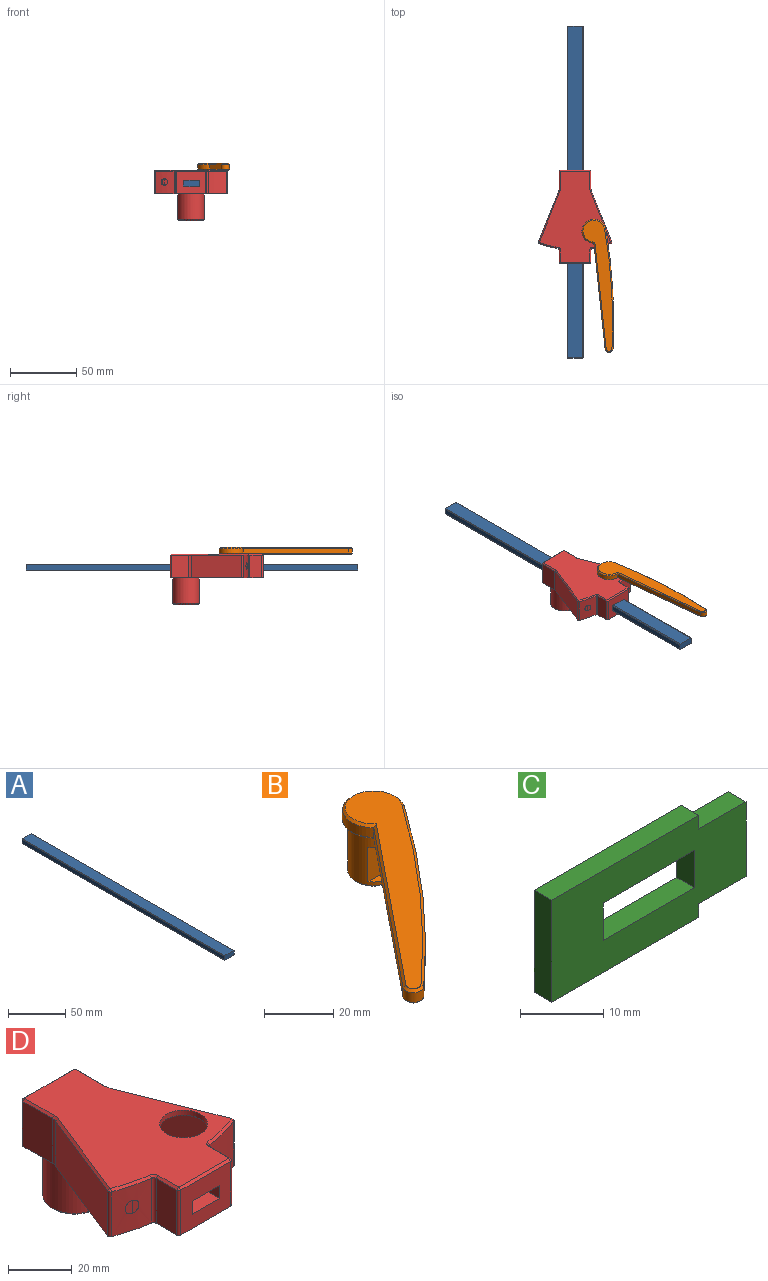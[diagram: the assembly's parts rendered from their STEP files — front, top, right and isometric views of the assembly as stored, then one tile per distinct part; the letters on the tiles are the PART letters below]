
ASSEMBLY  parts=4 mates=3
PART A: 10 faces, bbox 12x250x5 mm
  f0: plane 250x11mm, normal (0,0,-1), area 2750mm2, adj f4,f5,f6,f9
  f1: plane 250x4mm, normal (1,0,0), area 1000mm2, adj f4,f5,f6,f7
  f2: plane 250x11mm, normal (0,0,1), area 2750mm2, adj f4,f5,f7,f8
  f3: plane 250x4mm, normal (-1,0,0), area 1000mm2, adj f4,f5,f8,f9
  f4: plane 12x5mm, normal (0,-1,0), area 59.8mm2, adj f0,f1,f2,f3,f6,f7,f8,f9
  f5: plane 12x5mm, normal (0,1,0), area 59.8mm2, adj f0,f1,f2,f3,f6,f7,f8,f9
  f6: cylinder r=0.5mm len=250mm, axis (0,-1,0), area 196.3mm2, adj f0,f1,f4,f5
  f7: cylinder r=0.5mm len=250mm, axis (0,1,0), area 196.3mm2, adj f1,f2,f4,f5
  f8: cylinder r=0.5mm len=250mm, axis (0,-1,0), area 196.3mm2, adj f2,f3,f4,f5
  f9: cylinder r=0.5mm len=250mm, axis (0,1,0), area 196.3mm2, adj f0,f3,f4,f5
PART B: 21 faces, bbox 66.3x82.5x23 mm
  f0: cylinder r=7.5mm len=17.2mm, axis (0,0,1), area 437mm2, adj f2,f3,f4,f5,f11,f16
  f1: plane 13.4x13.4mm, normal (0,0,-1), area 141mm2, adj f16
  f2: plane 12x6.34mm, normal (0,-1,0), area 76.1mm2, adj f0,f3,f4,f5
  f3: cylinder r=5.75mm len=12mm, axis (0,0,-1), area 216.8mm2, adj f0,f2,f4,f5
  f4: plane 15x13.84mm, normal (0,0,-1), area 52.1mm2, adj f0,f2,f3
  f5: plane 15x13.84mm, normal (0,0,1), area 52.1mm2, adj f0,f2,f3
  f6: cylinder r=400mm len=67.53mm, axis (0,0,-1), area 307.1mm2, adj f7,f9,f12,f20
  f7: cylinder r=9mm len=18mm, axis (0,0,-1), area 138.9mm2, adj f6,f8,f14,f18
  f8: plane 62.22x50.29mm, normal (-0.78,0.63,0), area 272mm2, adj f7,f9,f15,f17
  f9: cylinder r=3mm len=5.01mm, axis (0,0,-1), area 30.4mm2, adj f6,f8,f13,f19
  f10: plane 80.87x64.72mm, normal (0,0,1), area 881.8mm2, adj f17,f18,f19,f20
  f11: plane 80.87x64.72mm, normal (0,0,-1), area 705.1mm2, adj f0,f12,f13,f14,f15
  f12: cone r=399.2mm half-angle=45deg, axis (0,0,1), area 102.1mm2, adj f6,f11,f13,f14
  f13: cone r=2.2mm half-angle=45deg, axis (0,0,1), area 8.8mm2, adj f9,f11,f12,f15
  f14: cone r=9mm half-angle=45deg, axis (0,0,1), area 44.6mm2, adj f7,f11,f12,f15
  f15: plane 62.8x51.38mm, normal (-0.55,0.44,-0.71), area 90.9mm2, adj f8,f11,f13,f14
  f16: cone r=7.5mm half-angle=45deg, axis (0,0,1), area 50.5mm2, adj f0,f1
  f17: plane 62.8x51.38mm, normal (-0.55,0.44,0.71), area 90.9mm2, adj f8,f10,f18,f19
  f18: cone r=8.2mm half-angle=45deg, axis (0,0,-1), area 44.6mm2, adj f7,f10,f17,f20
  f19: cone r=3mm half-angle=45deg, axis (0,0,-1), area 8.8mm2, adj f9,f10,f17,f20
  f20: cone r=400mm half-angle=45deg, axis (0,0,-1), area 102.1mm2, adj f6,f10,f18,f19
PART C: 14 faces, bbox 33x3x15 mm
  f0: plane 15.5x3mm, normal (0,0,-1), area 46.5mm2, adj f1,f11,f12,f13
  f1: plane 5.5x3mm, normal (-1,0,0), area 16.5mm2, adj f0,f2,f12,f13
  f2: plane 15.5x3mm, normal (0,0,1), area 46.5mm2, adj f1,f11,f12,f13
  f3: plane 25x3mm, normal (0,0,-1), area 75mm2, adj f4,f10,f12,f13
  f4: plane 3x2mm, normal (1,0,0), area 6mm2, adj f3,f5,f12,f13
  f5: plane 8x3mm, normal (0,0,-1), area 24mm2, adj f4,f6,f12,f13
  f6: plane 11x3mm, normal (1,0,0), area 33mm2, adj f5,f7,f12,f13
  f7: plane 8x3mm, normal (0,0,1), area 24mm2, adj f6,f8,f12,f13
  f8: plane 3x2mm, normal (1,0,0), area 6mm2, adj f7,f9,f12,f13
  f9: plane 25x3mm, normal (0,0,1), area 75mm2, adj f8,f10,f12,f13
  f10: plane 15x3mm, normal (-1,0,0), area 45mm2, adj f3,f9,f12,f13
  f11: plane 5.5x3mm, normal (1,0,0), area 16.5mm2, adj f0,f2,f12,f13
  f12: plane 33x15mm, normal (0,-1,0), area 377.7mm2, adj f0,f1,f2,f3,f4,f5,f6,f7
  f13: plane 33x15mm, normal (0,1,0), area 377.7mm2, adj f0,f1,f2,f3,f4,f5,f6,f7
PART D: 63 faces, bbox 55.6x70.3x38.3 mm
  f0: cylinder r=80mm len=17.2mm, axis (0,0,-1), area 232.7mm2, adj f7,f30,f31,f33,f38,f46
  f1: plane 16x4.49mm, normal (0,1,0), area 71.8mm2, adj f2,f7,f17,f29
  f2: plane 7.79x4.49mm, normal (0,0,-1), area 11.4mm2, adj f1,f17,f29
  f3: plane 22x17.2mm, normal (0,-1,0), area 318.4mm2, adj f7,f23,f24,f25,f26,f34,f37,f45
  f4: plane 22x17.2mm, normal (0,1,0), area 318.4mm2, adj f7,f19,f20,f21,f22,f35,f36,f58
  f5: plane 33.09x16.26mm, normal (0,1,0), area 439.1mm2, adj f7,f16,f18,f23,f24,f25,f26,f29
  f6: plane 26.09x16mm, normal (0,-1,0), area 357.5mm2, adj f7,f16,f17,f18,f19,f20,f21,f22
  f7: plane 70x55.38mm, normal (0,0,-1), area 1017.3mm2, adj f0,f1,f3,f4,f5,f6,f8,f9
  f8: cylinder r=80mm len=17.2mm, axis (0,0,-1), area 252.4mm2, adj f7,f32,f39,f53
  f9: plane 38.15x17.2mm, normal (0.93,0.37,0), area 706.7mm2, adj f7,f39,f40,f57
  f10: plane 38.15x17.2mm, normal (-0.93,0.37,0), area 706.7mm2, adj f7,f38,f41,f50
  f11: plane 68.4x53.78mm, normal (0,0,1), area 2047.7mm2, adj f29,f42,f43,f44,f45,f46,f47,f48
  f12: plane 17.2x8.99mm, normal (1,0,0), area 154.6mm2, adj f7,f32,f34,f49
  f13: plane 17.2x8.99mm, normal (-1,0,0), area 154.6mm2, adj f7,f33,f37,f42
  f14: plane 17.2x13.04mm, normal (1,0,0), area 224.2mm2, adj f7,f35,f40,f61
  f15: plane 17.2x13.04mm, normal (-1,0,0), area 224.2mm2, adj f7,f36,f41,f54
  f16: plane 28x16mm, normal (0.93,-0.37,0), area 482.5mm2, adj f5,f6,f7,f18
  f17: plane 28x16mm, normal (-0.93,-0.37,0), area 482.5mm2, adj f1,f2,f6,f7,f18
  f18: plane 45.38x28mm, normal (0,0,-1), area 875.4mm2, adj f5,f6,f16,f17,f29
  f19: plane 23x5mm, normal (1,0,0), area 115mm2, adj f4,f6,f20,f22
  f20: plane 23x12mm, normal (0,0,-1), area 276mm2, adj f4,f6,f19,f21
  f21: plane 23x5mm, normal (-1,0,0), area 115mm2, adj f4,f6,f20,f22
  f22: plane 23x12mm, normal (0,0,1), area 276mm2, adj f4,f6,f19,f21
  f23: plane 19x12mm, normal (0,0,1), area 228mm2, adj f3,f5,f24,f26
  f24: plane 19x5mm, normal (-1,0,0), area 95mm2, adj f3,f5,f23,f25
  f25: plane 19x12mm, normal (0,0,-1), area 228mm2, adj f3,f5,f24,f26
  f26: plane 19x5mm, normal (1,0,0), area 95mm2, adj f3,f5,f23,f25
  f27: cylinder r=10mm len=20mm, axis (0,0,1), area 1206.4mm2, adj f7,f62
  f28: plane 18.4x18.4mm, normal (0,0,-1), area 265.9mm2, adj f62
  f29: cylinder r=7.5mm len=18mm, axis (0,0,-1), area 296.1mm2, adj f1,f2,f5,f7,f11,f18
  f30: cone r=2.5mm half-angle=3deg, axis (0.21,0.98,0), area 111.5mm2, adj f0,f5,f31
  f31: cylinder r=2.5mm len=5mm, axis (-0.21,-0.98,0), area 0mm2, adj f0,f30
  f32: cylinder r=1mm len=17.2mm, axis (0,0,-1), area 24.2mm2, adj f7,f8,f12,f51
  f33: cylinder r=1mm len=17.2mm, axis (0,0,-1), area 24.2mm2, adj f0,f7,f13,f44
  f34: cylinder r=1mm len=17.2mm, axis (0,0,1), area 27mm2, adj f3,f7,f12,f47
  f35: cylinder r=1mm len=17.2mm, axis (0,0,-1), area 27mm2, adj f4,f7,f14,f60
  f36: cylinder r=1mm len=17.2mm, axis (0,0,1), area 27mm2, adj f4,f7,f15,f56
  f37: cylinder r=1mm len=17.2mm, axis (0,0,-1), area 27mm2, adj f3,f7,f13,f43
  f38: cylinder r=1mm len=17.2mm, axis (0,0,-1), area 27.6mm2, adj f0,f7,f10,f48
  f39: cylinder r=1mm len=17.2mm, axis (0,0,-1), area 27.6mm2, adj f7,f8,f9,f55
  f40: cylinder r=5mm len=17.2mm, axis (0,0,1), area 32.7mm2, adj f7,f9,f14,f59
  f41: cylinder r=5mm len=17.2mm, axis (0,0,1), area 32.7mm2, adj f7,f10,f15,f52
  f42: plane 8.99x0.8mm, normal (-0.71,0,0.71), area 10.2mm2, adj f11,f13,f43,f44
  f43: cone r=0.2mm half-angle=45deg, axis (0,0,-1), area 1.1mm2, adj f11,f37,f42,f45
  f44: cone r=1.8mm half-angle=45deg, axis (0,0,1), area 2.2mm2, adj f11,f33,f42,f46
  f45: plane 22x0.8mm, normal (0,-0.71,0.71), area 24.9mm2, adj f3,f11,f43,f47
  f46: cone r=79.2mm half-angle=45deg, axis (0,0,-1), area 16.5mm2, adj f0,f11,f44,f48
  f47: cone r=0.2mm half-angle=45deg, axis (0,0,-1), area 1.1mm2, adj f11,f34,f45,f49
  f48: cone r=0.2mm half-angle=45deg, axis (0,0,-1), area 1.1mm2, adj f11,f38,f46,f50
  f49: plane 8.99x0.8mm, normal (0.71,0,0.71), area 10.2mm2, adj f11,f12,f47,f51
  f50: plane 38.45x16mm, normal (-0.66,0.26,0.71), area 46.5mm2, adj f10,f11,f48,f52
  f51: cone r=1.8mm half-angle=45deg, axis (0,0,1), area 2.2mm2, adj f11,f32,f49,f53
  f52: cone r=5.8mm half-angle=45deg, axis (0,0,1), area 2.3mm2, adj f11,f41,f50,f54
  f53: cone r=79.2mm half-angle=45deg, axis (0,0,-1), area 16.5mm2, adj f8,f11,f51,f55
  f54: plane 13.04x0.8mm, normal (-0.71,0,0.71), area 14.7mm2, adj f11,f15,f52,f56
  f55: cone r=0.2mm half-angle=45deg, axis (0,0,-1), area 1.1mm2, adj f11,f39,f53,f57
  f56: cone r=0.2mm half-angle=45deg, axis (0,0,-1), area 1.1mm2, adj f11,f36,f54,f58
  f57: plane 38.45x16mm, normal (0.66,0.26,0.71), area 46.5mm2, adj f9,f11,f55,f59
  f58: plane 22x0.8mm, normal (0,0.71,0.71), area 24.9mm2, adj f4,f11,f56,f60
  f59: cone r=5.8mm half-angle=45deg, axis (0,0,1), area 2.3mm2, adj f11,f40,f57,f61
  f60: cone r=0.2mm half-angle=45deg, axis (0,0,-1), area 1.1mm2, adj f11,f35,f58,f61
  f61: plane 13.04x0.8mm, normal (0.71,0,0.71), area 14.7mm2, adj f11,f14,f59,f60
  f62: cone r=9.2mm half-angle=45deg, axis (0,0,1), area 68.2mm2, adj f27,f28
PLACE A t=(0,143.53,8)mm
PLACE B rot(axis=(0,0,1),45deg) t=(14.17,-11,18)mm
PLACE C t=(0,-0.5,8)mm
PLACE D at identity fixed
MATE slider C.f12 <-> A.f5  axis (0,-1,0) through (0,-3.5,8)mm
MATE revolute D.f29 <-> B.f0  axis (0,0,1) through (14.17,-11,18)mm
MATE slider D.f3 <-> A.f5  axis (0,-1,0) through (0,-35,8)mm
